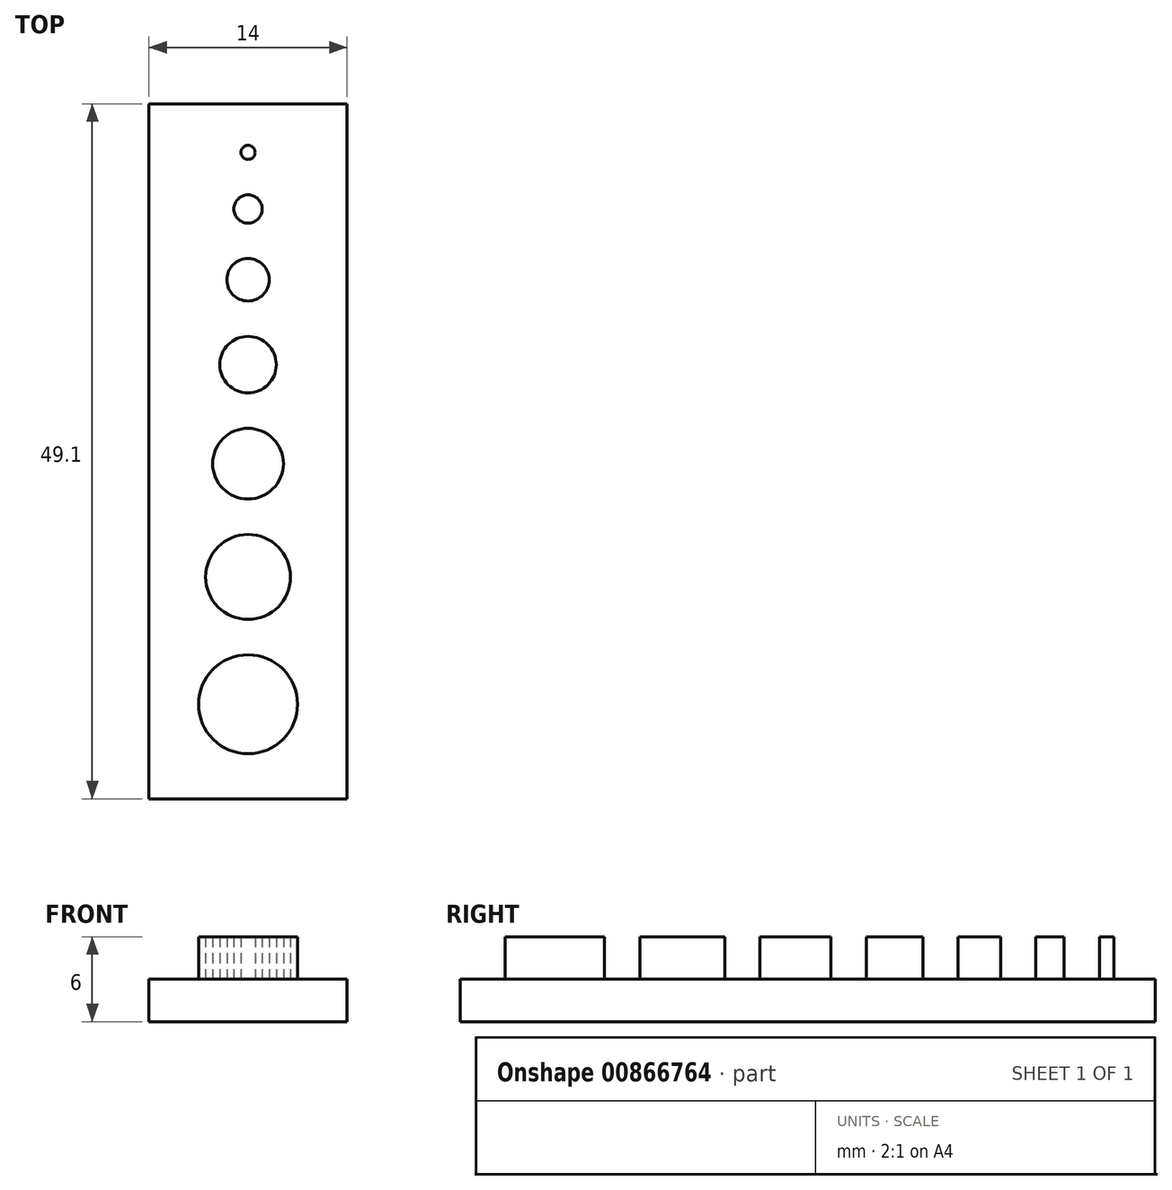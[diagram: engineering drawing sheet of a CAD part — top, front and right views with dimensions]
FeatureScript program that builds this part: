
annotation { "Feature Type Name" : "Feature", "Feature Type Description" : "" }
export const myFeature = defineFeature(function(context is Context, id is Id, definition is map)
    precondition{}
    {
        {
            var Q0;
            Q0=qCreatedBy(makeId("Top.planeOp"),FACE);
            var sketch = newSketch(context, id + "F0", { "sketchPlane" : qUnion([Q0])});
            skCircle(sketch, "E0", {"center": v(0, 12.3) * mm, "radius": 0.5 * mm});
            skCircle(sketch, "E1", {"center": v(0, 8.3) * mm, "radius": 1 * mm});
            skCircle(sketch, "E2", {"center": v(0, 3.3) * mm, "radius": 1.5 * mm});
            skCircle(sketch, "E3", {"center": v(0, -2.7) * mm, "radius": 2 * mm});
            skCircle(sketch, "E4", {"center": v(0, -9.7) * mm, "radius": 2.5 * mm});
            skCircle(sketch, "E5", {"center": v(0, -17.7) * mm, "radius": 3 * mm});
            skCircle(sketch, "E6", {"center": v(0, -26.7) * mm, "radius": 3.5 * mm});
            skLineSegment(sketch, "E7.bottom", {"start": v(-7, 15.73) * mm, "end": v(7, 15.73) * mm});
            skLineSegment(sketch, "E7.top", {"start": v(-7, -33.37) * mm, "end": v(7, -33.37) * mm});
            skLineSegment(sketch, "E7.left", {"start": v(-7, 15.73) * mm, "end": v(-7, -33.37) * mm});
            skLineSegment(sketch, "E7.right", {"start": v(7, 15.73) * mm, "end": v(7, -33.37) * mm});
            skSolve(sketch);
        }
        {
            var Q0;
            Q0=makeQuery(id+"F0.imprint","IMPRINT",FACE,{"disambiguationData":[TD([[makeQuery(id+"F0.imprint","IMPRINT",EDGE,{"derivedFrom":sQuery(id+"F0.wireOp",EDGE,"E0")}),-1.0]])]});
            extrude(context, id + "F1", {"entities" : qUnion([Q0]), "depth" : 3 * mm, "offsetDistance" : 25 * mm});
        }
        {
            var Q0;
            Q0=makeQuery(id+"F0.imprint","IMPRINT",FACE,{"disambiguationData":[TD([[makeQuery(id+"F0.imprint","IMPRINT",EDGE,{"derivedFrom":sQuery(id+"F0.wireOp",EDGE,"E6")}),1.0]])]});
            var Q1;
            Q1=makeQuery(id+"F0.imprint","IMPRINT",FACE,{"disambiguationData":[TD([[makeQuery(id+"F0.imprint","IMPRINT",EDGE,{"derivedFrom":sQuery(id+"F0.wireOp",EDGE,"E5")}),1.0]])]});
            var Q2;
            Q2=makeQuery(id+"F0.imprint","IMPRINT",FACE,{"disambiguationData":[TD([[makeQuery(id+"F0.imprint","IMPRINT",EDGE,{"derivedFrom":sQuery(id+"F0.wireOp",EDGE,"E4")}),1.0]])]});
            var Q3;
            Q3=makeQuery(id+"F0.imprint","IMPRINT",FACE,{"disambiguationData":[TD([[makeQuery(id+"F0.imprint","IMPRINT",EDGE,{"derivedFrom":sQuery(id+"F0.wireOp",EDGE,"E3")}),1.0]])]});
            var Q4;
            Q4=makeQuery(id+"F0.imprint","IMPRINT",FACE,{"disambiguationData":[TD([[makeQuery(id+"F0.imprint","IMPRINT",EDGE,{"derivedFrom":sQuery(id+"F0.wireOp",EDGE,"E2")}),1.0]])]});
            var Q5;
            Q5=makeQuery(id+"F0.imprint","IMPRINT",FACE,{"disambiguationData":[TD([[makeQuery(id+"F0.imprint","IMPRINT",EDGE,{"derivedFrom":sQuery(id+"F0.wireOp",EDGE,"E1")}),1.0]])]});
            var Q6;
            Q6=makeQuery(id+"F0.imprint","IMPRINT",FACE,{"disambiguationData":[TD([[makeQuery(id+"F0.imprint","IMPRINT",EDGE,{"derivedFrom":sQuery(id+"F0.wireOp",EDGE,"E0")}),1.0]])]});
            extrude(context, id + "F2", {"entities" : qUnion([Q0, Q1, Q2, Q3, Q4, Q5, Q6]), "operationType" : NewBodyOperationType.ADD, "depth" : 6 * mm, "offsetDistance" : 25 * mm});
        }
    });
